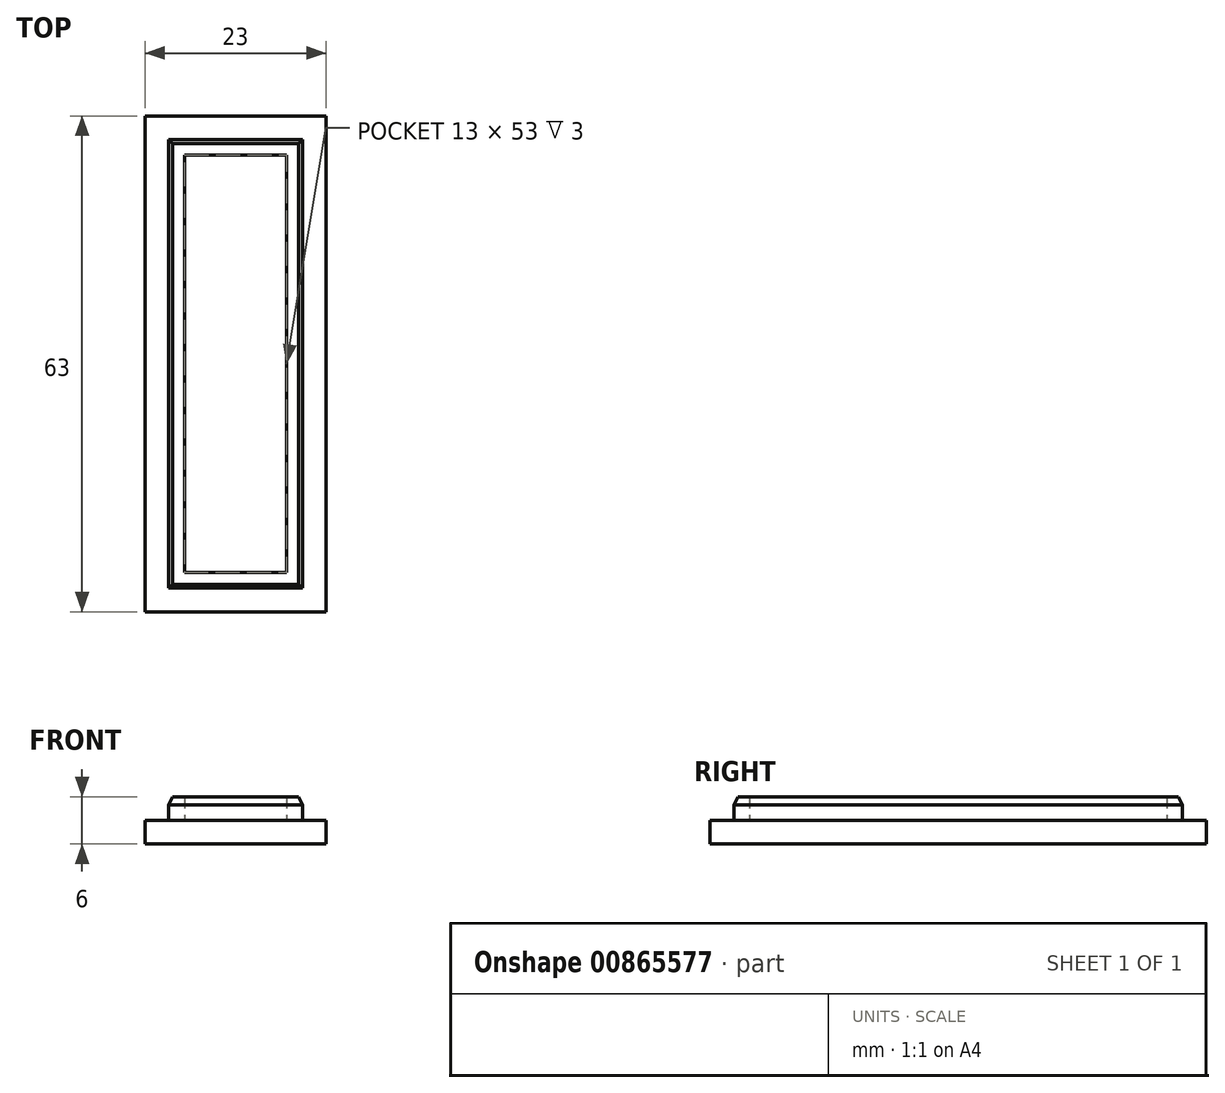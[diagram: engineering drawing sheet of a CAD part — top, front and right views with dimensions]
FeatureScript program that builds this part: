
annotation { "Feature Type Name" : "Feature", "Feature Type Description" : "" }
export const myFeature = defineFeature(function(context is Context, id is Id, definition is map)
    precondition{}
    {
        {
            var Q0;
            Q0=qCreatedBy(makeId("Top.planeOp"),FACE);
            var sketch = newSketch(context, id + "F0", { "sketchPlane" : qUnion([Q0])});
            skLineSegment(sketch, "E0.bottom", {"start": v(0, 0) * mm, "end": v(23, 0) * mm});
            skLineSegment(sketch, "E0.top", {"start": v(0, 63) * mm, "end": v(23, 63) * mm});
            skLineSegment(sketch, "E0.left", {"start": v(0, 0) * mm, "end": v(0, 63) * mm});
            skLineSegment(sketch, "E0.right", {"start": v(23, 0) * mm, "end": v(23, 63) * mm});
            skSolve(sketch);
        }
        {
            var Q0;
            Q0 = qSketchRegion(id + "F0", true);
            extrude(context, id + "F1", {"entities" : qUnion([Q0]), "depth" : 3 * mm, "offsetDistance" : 25.4 * mm});
        }
        {
            var Q0;
            Q0=makeQuery(id+"F1.opExtrude","CAP_FACE",FACE,{"disambiguationData":[OSD([sQuery(id+"F0.wireOp",EDGE,"E0.bottom"),sQuery(id+"F0.wireOp",EDGE,"E0.top"),sQuery(id+"F0.wireOp",EDGE,"E0.left"),sQuery(id+"F0.wireOp",EDGE,"E0.right")])],"isStart":true});
            var sketch = newSketch(context, id + "F2", { "sketchPlane" : qUnion([Q0])});
            skLineSegment(sketch, "E1.bottom", {"start": v(20, -60) * mm, "end": v(3, -60) * mm});
            skLineSegment(sketch, "E1.top", {"start": v(20, -3) * mm, "end": v(3, -3) * mm});
            skLineSegment(sketch, "E1.left", {"start": v(20, -60) * mm, "end": v(20, -3) * mm});
            skLineSegment(sketch, "E1.right", {"start": v(3, -60) * mm, "end": v(3, -3) * mm});
            skLineSegment(sketch, "E2.bottom", {"start": v(18, -58) * mm, "end": v(5, -58) * mm});
            skLineSegment(sketch, "E2.top", {"start": v(18, -5) * mm, "end": v(5, -5) * mm});
            skLineSegment(sketch, "E2.left", {"start": v(18, -58) * mm, "end": v(18, -5) * mm});
            skLineSegment(sketch, "E2.right", {"start": v(5, -58) * mm, "end": v(5, -5) * mm});
            skSolve(sketch);
        }
        {
            var Q0;
            Q0 = qSketchRegion(id + "F2", true);
            extrude(context, id + "F3", {"entities" : qUnion([Q0]), "operationType" : NewBodyOperationType.ADD, "oppositeDirection" : true, "depth" : 6 * mm, "offsetDistance" : 25.4 * mm});
        }
        {
            var Q0;
            Q0=makeQuery(id+"F3.opExtrude","CAP_EDGE",EDGE,{"disambiguationData":[OSD([sQuery(id+"F2.wireOp",EDGE,"E1.top")])],"isStart":false});
            var Q1;
            Q1=makeQuery(id+"F3.opExtrude","CAP_EDGE",EDGE,{"disambiguationData":[OSD([sQuery(id+"F2.wireOp",EDGE,"E1.left")])],"isStart":false});
            var Q2;
            Q2=makeQuery(id+"F3.opExtrude","CAP_EDGE",EDGE,{"disambiguationData":[OSD([sQuery(id+"F2.wireOp",EDGE,"E1.right")])],"isStart":false});
            var Q3;
            Q3=makeQuery(id+"F3.opExtrude","CAP_EDGE",EDGE,{"disambiguationData":[OSD([sQuery(id+"F2.wireOp",EDGE,"E1.bottom")])],"isStart":false});
            chamfer(context, id + "F4", {"entities" : qUnion([Q0, Q1, Q2, Q3]), "chamferType" : ChamferType.TWO_OFFSETS, "width1" : 1 * mm, "oppositeDirection" : false, "width2" : 0.5 * mm, "tangentPropagation" : true});
        }
    });
